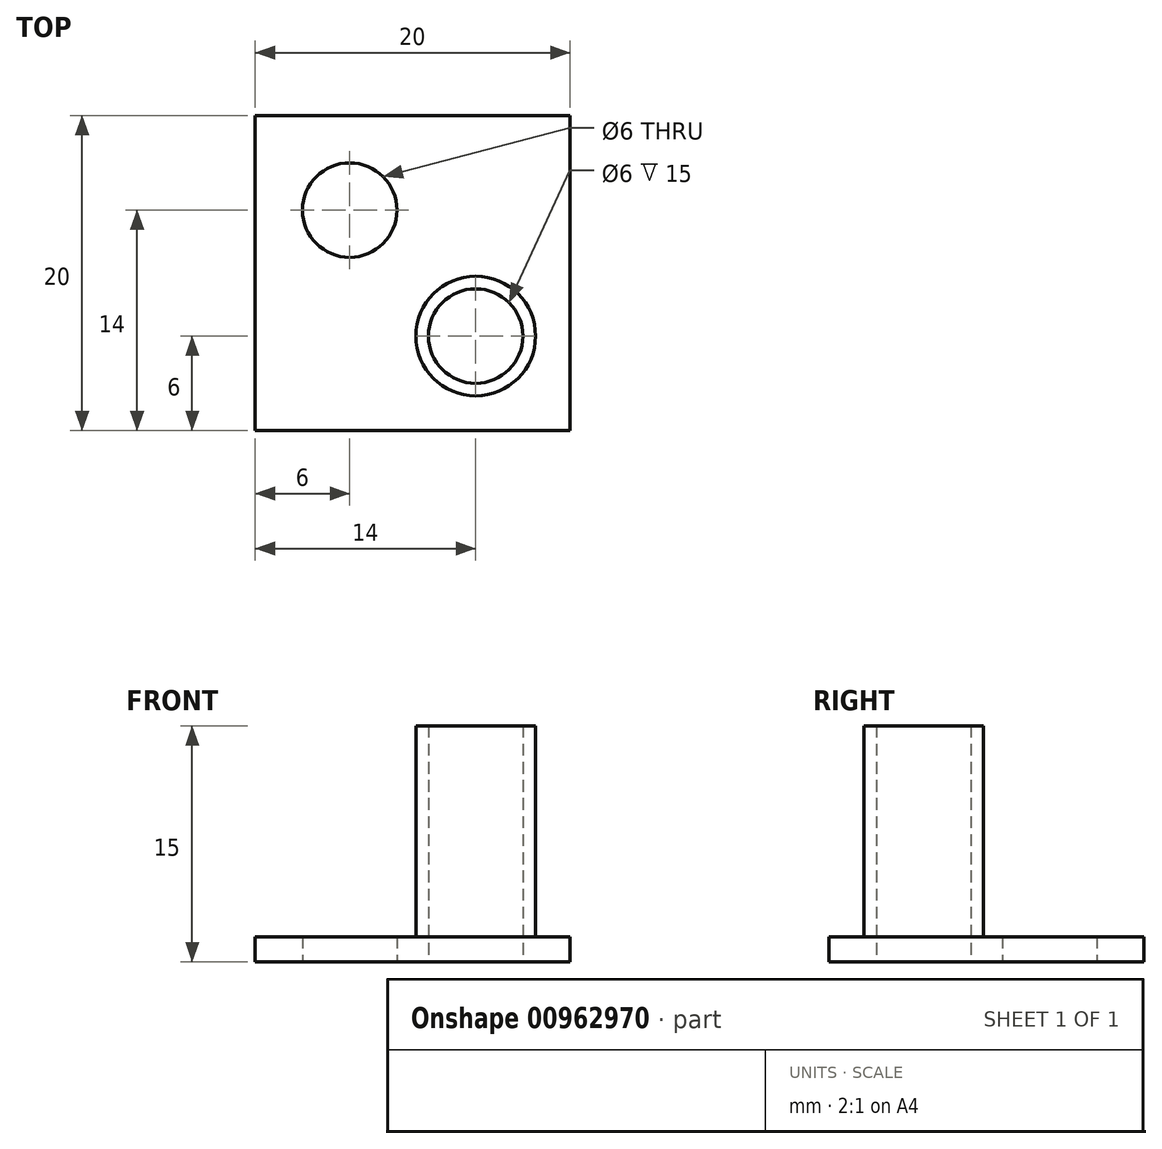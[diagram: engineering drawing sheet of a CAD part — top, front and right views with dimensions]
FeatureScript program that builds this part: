
annotation { "Feature Type Name" : "Feature", "Feature Type Description" : "" }
export const myFeature = defineFeature(function(context is Context, id is Id, definition is map)
    precondition{}
    {
        {
            var Q0;
            Q0=qCreatedBy(makeId("Top.planeOp"),FACE);
            var sketch = newSketch(context, id + "F0", { "sketchPlane" : qUnion([Q0])});
            skLineSegment(sketch, "E0.bottom", {"start": v(0, 0) * mm, "end": v(20, 0) * mm});
            skLineSegment(sketch, "E0.top", {"start": v(0, -20) * mm, "end": v(20, -20) * mm});
            skLineSegment(sketch, "E0.left", {"start": v(0, 0) * mm, "end": v(0, -20) * mm});
            skLineSegment(sketch, "E0.right", {"start": v(20, 0) * mm, "end": v(20, -20) * mm});
            skCircle(sketch, "E1", {"center": v(6, -6) * mm, "radius": 3 * mm});
            skLineSegment(sketch, "E2", {"start": v(0, -20) * mm, "end": v(20, 0) * mm});
            skLineSegment(sketch, "E3", {"start": v(6, -6) * mm, "end": v(10, -10) * mm});
            skLineSegment(sketch, "E4.MirrorCS", {"start": v(14, -14) * mm, "end": v(10, -10) * mm});
            skCircle(sketch, "E5", {"center": v(14, -14) * mm, "radius": 3 * mm});
            skCircle(sketch, "E6", {"center": v(14, -14) * mm, "radius": 3.8 * mm});
            skSolve(sketch);
        }
        {
            var Q0;
            {var subQ3=sQuery(id+"F0.wireOp",EDGE,"E0.bottom");Q0=makeQuery(id+"F0.imprint","IMPRINT",FACE,{"disambiguationData":[TD([[makeQuery(id+"F0.imprint","IMPRINT",EDGE,{"derivedFrom":subQ3}),-1.0]])]});}
            var Q1;
            {var subQ1=sQuery(id+"F0.wireOp",EDGE,"E0.top");Q1=makeQuery(id+"F0.imprint","IMPRINT",FACE,{"disambiguationData":[TD([[makeQuery(id+"F0.imprint","IMPRINT",EDGE,{"derivedFrom":subQ1}),1.0]])]});}
            extrude(context, id + "F1", {"entities" : qUnion([Q0, Q1]), "depth" : 1.6 * mm, "offsetDistance" : 25 * mm});
        }
        {
            var Q0;
            Q0=makeQuery(id+"F0.imprint","IMPRINT",FACE,{"disambiguationData":[TD([[makeQuery(id+"F0.imprint","IMPRINT",EDGE,{"derivedFrom":sQuery(id+"F0.wireOp",EDGE,"E5")}),-1.0]])]});
            extrude(context, id + "F2", {"entities" : qUnion([Q0]), "operationType" : NewBodyOperationType.ADD, "depth" : 15 * mm, "offsetDistance" : 25 * mm});
        }
    });
